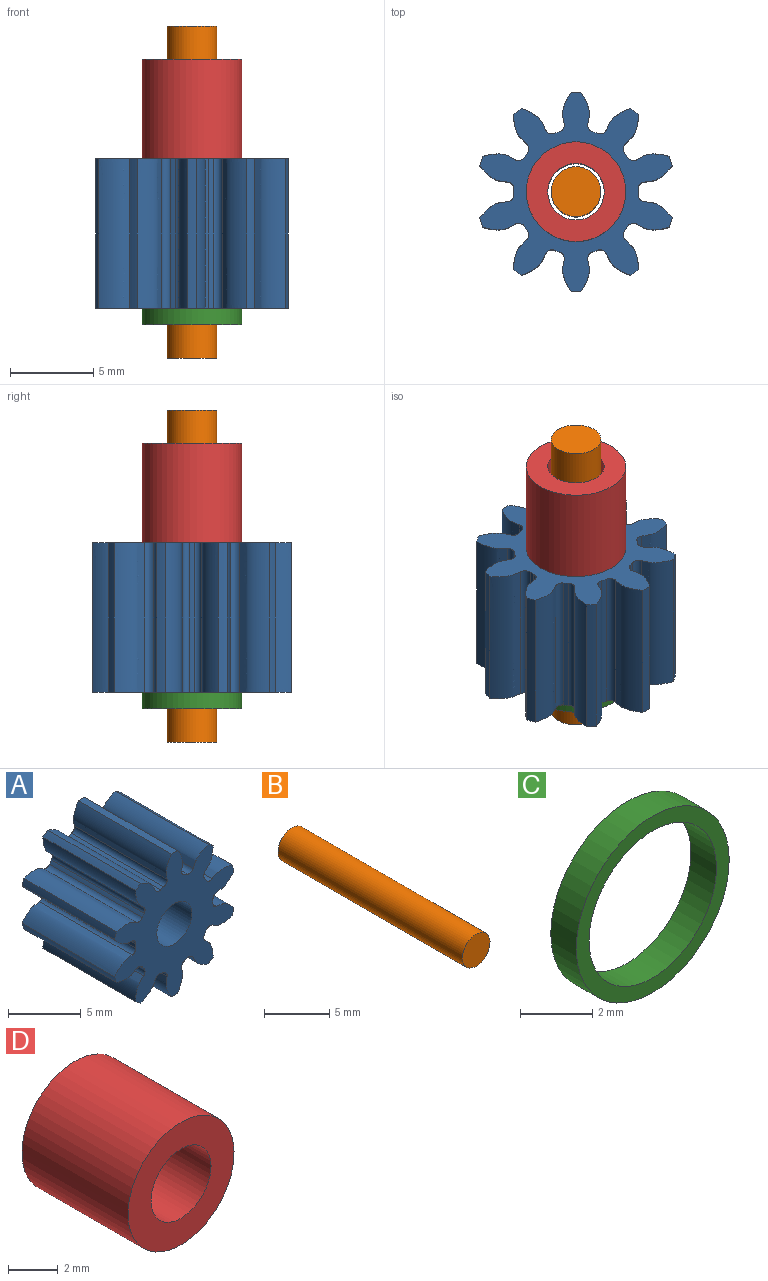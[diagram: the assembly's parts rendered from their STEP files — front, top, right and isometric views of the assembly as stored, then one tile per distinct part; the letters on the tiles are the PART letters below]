
ASSEMBLY  parts=4 mates=3
PART A: 63 faces, bbox 11.6x9x12 mm
  f0: cylinder r=6mm len=9mm, axis (0,1,0), area 5.3mm2, adj f9,f11,f52,f59
  f1: cylinder r=6mm len=9mm, axis (0,1,0), area 5.3mm2, adj f9,f11,f12,f54
  f2: cylinder r=6mm len=9mm, axis (0,1,0), area 5.3mm2, adj f9,f11,f42,f49
  f3: cylinder r=6mm len=9mm, axis (0,1,0), area 5.3mm2, adj f9,f11,f44,f57
  f4: cylinder r=6mm len=9mm, axis (0,1,0), area 5.3mm2, adj f9,f11,f32,f39
  f5: cylinder r=6mm len=9mm, axis (0,1,0), area 5.3mm2, adj f9,f11,f27,f34
  f6: cylinder r=6mm len=9mm, axis (0,1,0), area 5.3mm2, adj f9,f11,f22,f29
  f7: cylinder r=6mm len=9mm, axis (0,1,0), area 5.3mm2, adj f9,f11,f24,f47
  f8: cylinder r=6mm len=9mm, axis (0,1,0), area 5.3mm2, adj f9,f11,f19,f37
  f9: plane 12.02x11.61mm, normal (0,-1,0), area 66mm2, adj f0,f1,f2,f3,f4,f5,f6,f7
  f10: cylinder r=6mm len=9mm, axis (0,1,0), area 5.3mm2, adj f9,f11,f14,f17
  f11: plane 12.02x11.61mm, normal (0,1,0), area 66mm2, adj f0,f1,f2,f3,f4,f5,f6,f7
  f12: extruded ~9x1.69mm, area 18.3mm2, adj f1,f9,f11,f15
  f13: cylinder r=3.75mm len=9mm, axis (0,1,0), area 2.9mm2, adj f9,f11,f15,f16
  f14: extruded ~9x1.69mm, area 18.3mm2, adj f9,f10,f11,f16
  f15: cylinder r=0.41mm len=9mm, axis (0,1,0), area 5.5mm2, adj f9,f11,f12,f13
  f16: cylinder r=0.41mm len=9mm, axis (0,1,0), area 5.5mm2, adj f9,f11,f13,f14
  f17: extruded ~9x1.95mm, area 18.3mm2, adj f9,f10,f11,f20
  f18: cylinder r=3.75mm len=9mm, axis (0,1,0), area 2.9mm2, adj f9,f11,f20,f21
  f19: extruded ~9x1.79mm, area 18.3mm2, adj f8,f9,f11,f21
  f20: cylinder r=0.41mm len=9mm, axis (0,1,0), area 5.5mm2, adj f9,f11,f17,f18
  f21: cylinder r=0.41mm len=9mm, axis (0,1,0), area 5.5mm2, adj f9,f11,f18,f19
  f22: extruded ~9x1.69mm, area 18.3mm2, adj f6,f9,f11,f25
  f23: cylinder r=3.75mm len=9mm, axis (0,1,0), area 2.9mm2, adj f9,f11,f25,f26
  f24: extruded ~9x1.69mm, area 18.3mm2, adj f7,f9,f11,f26
  f25: cylinder r=0.41mm len=9mm, axis (0,1,0), area 5.5mm2, adj f9,f11,f22,f23
  f26: cylinder r=0.41mm len=9mm, axis (0,1,0), area 5.5mm2, adj f9,f11,f23,f24
  f27: extruded ~9x1.79mm, area 18.3mm2, adj f5,f9,f11,f30
  f28: cylinder r=3.75mm len=9mm, axis (0,1,0), area 2.9mm2, adj f9,f11,f30,f31
  f29: extruded ~9x1.95mm, area 18.3mm2, adj f6,f9,f11,f31
  f30: cylinder r=0.41mm len=9mm, axis (0,1,0), area 5.5mm2, adj f9,f11,f27,f28
  f31: cylinder r=0.41mm len=9mm, axis (0,1,0), area 5.5mm2, adj f9,f11,f28,f29
  f32: extruded ~9x1.91mm, area 18.3mm2, adj f4,f9,f11,f35
  f33: cylinder r=3.75mm len=9mm, axis (0,1,0), area 2.9mm2, adj f9,f11,f35,f36
  f34: extruded ~9x1.46mm, area 18.3mm2, adj f5,f9,f11,f36
  f35: cylinder r=0.41mm len=9mm, axis (0,1,0), area 5.5mm2, adj f9,f11,f32,f33
  f36: cylinder r=0.41mm len=9mm, axis (0,1,0), area 5.5mm2, adj f9,f11,f33,f34
  f37: extruded ~9x1.46mm, area 18.3mm2, adj f8,f9,f11,f40
  f38: cylinder r=3.75mm len=9mm, axis (0,1,0), area 2.9mm2, adj f9,f11,f40,f41
  f39: extruded ~9x1.91mm, area 18.3mm2, adj f4,f9,f11,f41
  f40: cylinder r=0.41mm len=9mm, axis (0,1,0), area 5.5mm2, adj f9,f11,f37,f38
  f41: cylinder r=0.41mm len=9mm, axis (0,1,0), area 5.5mm2, adj f9,f11,f38,f39
  f42: extruded ~9x1.46mm, area 18.3mm2, adj f2,f9,f11,f45
  f43: cylinder r=3.75mm len=9mm, axis (0,1,0), area 2.9mm2, adj f9,f11,f45,f46
  f44: extruded ~9x1.91mm, area 18.3mm2, adj f3,f9,f11,f46
  f45: cylinder r=0.41mm len=9mm, axis (0,1,0), area 5.5mm2, adj f9,f11,f42,f43
  f46: cylinder r=0.41mm len=9mm, axis (0,1,0), area 5.5mm2, adj f9,f11,f43,f44
  f47: extruded ~9x1.95mm, area 18.3mm2, adj f7,f9,f11,f50
  f48: cylinder r=3.75mm len=9mm, axis (0,1,0), area 2.9mm2, adj f9,f11,f50,f51
  f49: extruded ~9x1.79mm, area 18.3mm2, adj f2,f9,f11,f51
  f50: cylinder r=0.41mm len=9mm, axis (0,1,0), area 5.5mm2, adj f9,f11,f47,f48
  f51: cylinder r=0.41mm len=9mm, axis (0,1,0), area 5.5mm2, adj f9,f11,f48,f49
  f52: extruded ~9x1.79mm, area 18.3mm2, adj f0,f9,f11,f55
  f53: cylinder r=3.75mm len=9mm, axis (0,1,0), area 2.9mm2, adj f9,f11,f55,f56
  f54: extruded ~9x1.95mm, area 18.3mm2, adj f1,f9,f11,f56
  f55: cylinder r=0.41mm len=9mm, axis (0,1,0), area 5.5mm2, adj f9,f11,f52,f53
  f56: cylinder r=0.41mm len=9mm, axis (0,1,0), area 5.5mm2, adj f9,f11,f53,f54
  f57: extruded ~9x1.91mm, area 18.3mm2, adj f3,f9,f11,f60
  f58: cylinder r=3.75mm len=9mm, axis (0,1,0), area 2.9mm2, adj f9,f11,f60,f61
  f59: extruded ~9x1.46mm, area 18.3mm2, adj f0,f9,f11,f61
  f60: cylinder r=0.41mm len=9mm, axis (0,1,0), area 5.5mm2, adj f9,f11,f57,f58
  f61: cylinder r=0.41mm len=9mm, axis (0,1,0), area 5.5mm2, adj f9,f11,f58,f59
  f62: cylinder r=1.7mm len=9mm, axis (0,-1,0), area 96.1mm2, adj f9,f11
PART B: 3 faces, bbox 3x20x3 mm
  f0: cylinder r=1.5mm len=20mm, axis (0,1,0), area 188.5mm2, adj f1,f2
  f1: plane 3x3mm, normal (0,-1,0), area 7.1mm2, adj f0
  f2: plane 3x3mm, normal (0,1,0), area 7.1mm2, adj f0
PART C: 4 faces, bbox 6x1x6 mm
  f0: cylinder r=2.5mm len=5mm, axis (0,1,0), area 15.7mm2, adj f2,f3
  f1: cylinder r=3mm len=6mm, axis (0,1,0), area 18.8mm2, adj f2,f3
  f2: plane 6x6mm, normal (0,-1,0), area 8.6mm2, adj f0,f1
  f3: plane 6x6mm, normal (0,1,0), area 8.6mm2, adj f0,f1
PART D: 4 faces, bbox 6x6x6 mm
  f0: cylinder r=1.7mm len=6mm, axis (0,1,0), area 64.1mm2, adj f2,f3
  f1: cylinder r=3mm len=6mm, axis (0,1,0), area 113.1mm2, adj f2,f3
  f2: plane 6x6mm, normal (0,-1,0), area 19.2mm2, adj f0,f1
  f3: plane 6x6mm, normal (0,1,0), area 19.2mm2, adj f0,f1
PLACE A rot(axis=(-1,0,0),90deg) t=(0,0,-7)mm
PLACE B rot(axis=(1,0,0),90deg) t=(0,0,10)mm
PLACE C rot(axis=(-1,0,0),90deg) t=(0,0,-8)mm
PLACE D rot(axis=(-1,0,0),90deg) t=(0,0,2)mm
MATE fastened A.f0 <-> C.f0  axis (0,0,-1) through (0,0,-7)mm
MATE fastened D.f1 <-> A.f0  axis (0,0,-1) through (0,0,2)mm
MATE fastened C.f1 <-> B.f0  axis (0,0,-1) through (0,0,-8)mm
